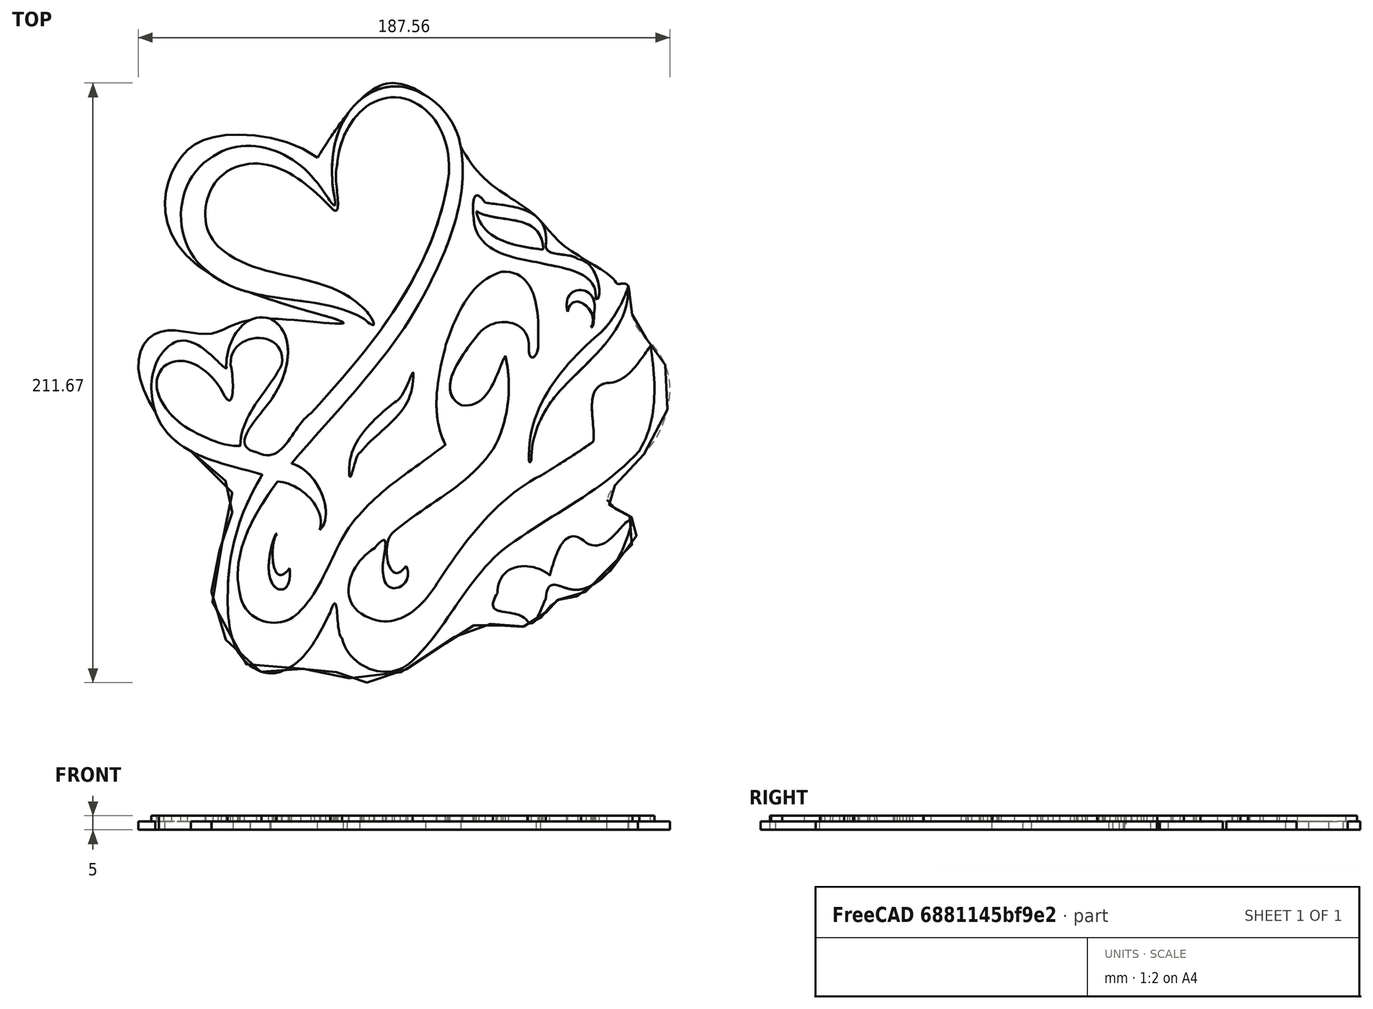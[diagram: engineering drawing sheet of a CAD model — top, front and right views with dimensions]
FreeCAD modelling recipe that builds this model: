
FCSTD DOCUMENT  (FreeCAD 0.20R29410 (Git))
Label: Miriam
License: All rights reserved
LicenseURL: http://en.wikipedia.org/wiki/All_rights_reserved
objects: Part::Feature×9, Sketcher::SketchObject×2, Part::Extrusion×2, PartDesign::Body×1, Part::MultiFuse×1, Mesh::Feature×1
note: 15 computed .brp shape members not serialized (recipe doc carries the construction recipe); baked Part::Feature solids carry a one-line shape summary decoded from their .brp

FEATURE [PartDesign::Body] Body
  Origin = -> Origin
FEATURE [Part::Feature] path198
  shape: bbox 180.5 x 215.9 x 2e-07 mm, 1 faces, 0 solids (baked)
FEATURE [Part::Feature] path198001
  shape: bbox 51.01 x 42.11 x 2e-07 mm, 1 faces, 0 solids (baked)
FEATURE [Part::Feature] path198002
  shape: bbox 53.62 x 39.98 x 2e-07 mm, 1 faces, 0 solids (baked)
FEATURE [Part::Feature] path198003
  shape: bbox 11.12 x 21.68 x 2e-07 mm, 1 faces, 0 solids (baked)
FEATURE [Part::Feature] path198004
  shape: bbox 23.9 x 49.31 x 2e-07 mm, 1 faces, 0 solids (baked)
FEATURE [Part::Feature] path198005
  shape: bbox 35.84 x 63.97 x 2e-07 mm, 1 faces, 0 solids (baked)
FEATURE [Part::Feature] path198006
  shape: bbox 14.27 x 15.77 x 2e-07 mm, 1 faces, 0 solids (baked)
FEATURE [Part::Feature] path198007
  shape: bbox 47.43 x 42.63 x 2e-07 mm, 1 faces, 0 solids (baked)
FEATURE [Part::Feature] path198008
  shape: bbox 23.68 x 13.52 x 2e-07 mm, 1 faces, 0 solids (baked)
FEATURE [Sketcher::SketchObject] Sketch
  FullyConstrained = false
  sketch-geometry (94):
    g0: BSplineCurve PolesCount=4 KnotsCount=2 Degree=3 IsPeriodic=0
    g1: BSplineCurve PolesCount=4 KnotsCount=2 Degree=3 IsPeriodic=0
    g2: BSplineCurve PolesCount=4 KnotsCount=2 Degree=3 IsPeriodic=0
    g3: BSplineCurve PolesCount=4 KnotsCount=2 Degree=3 IsPeriodic=0
    g4: BSplineCurve PolesCount=4 KnotsCount=2 Degree=3 IsPeriodic=0
    g5: BSplineCurve PolesCount=4 KnotsCount=2 Degree=3 IsPeriodic=0
    g6: BSplineCurve PolesCount=4 KnotsCount=2 Degree=3 IsPeriodic=0
    g7: BSplineCurve PolesCount=4 KnotsCount=2 Degree=3 IsPeriodic=0
    g8: BSplineCurve PolesCount=4 KnotsCount=2 Degree=3 IsPeriodic=0
    g9: BSplineCurve PolesCount=4 KnotsCount=2 Degree=3 IsPeriodic=0
    g10: BSplineCurve PolesCount=4 KnotsCount=2 Degree=3 IsPeriodic=0
    g11: BSplineCurve PolesCount=4 KnotsCount=2 Degree=3 IsPeriodic=0
    g12: BSplineCurve PolesCount=4 KnotsCount=2 Degree=3 IsPeriodic=0
    g13: BSplineCurve PolesCount=4 KnotsCount=2 Degree=3 IsPeriodic=0
    g14: BSplineCurve PolesCount=4 KnotsCount=2 Degree=3 IsPeriodic=0
    g15: BSplineCurve PolesCount=4 KnotsCount=2 Degree=3 IsPeriodic=0
    g16: BSplineCurve PolesCount=4 KnotsCount=2 Degree=3 IsPeriodic=0
    g17: BSplineCurve PolesCount=4 KnotsCount=2 Degree=3 IsPeriodic=0
    g18: BSplineCurve PolesCount=4 KnotsCount=2 Degree=3 IsPeriodic=0
    g19: BSplineCurve PolesCount=4 KnotsCount=2 Degree=3 IsPeriodic=0
    g20: BSplineCurve PolesCount=4 KnotsCount=2 Degree=3 IsPeriodic=0
    g21: BSplineCurve PolesCount=4 KnotsCount=2 Degree=3 IsPeriodic=0
    g22: BSplineCurve PolesCount=4 KnotsCount=2 Degree=3 IsPeriodic=0
    g23: BSplineCurve PolesCount=4 KnotsCount=2 Degree=3 IsPeriodic=0
    g24: BSplineCurve PolesCount=4 KnotsCount=2 Degree=3 IsPeriodic=0
    g25: BSplineCurve PolesCount=4 KnotsCount=2 Degree=3 IsPeriodic=0
    g26: BSplineCurve PolesCount=4 KnotsCount=2 Degree=3 IsPeriodic=0
    g27: BSplineCurve PolesCount=4 KnotsCount=2 Degree=3 IsPeriodic=0
    g28: BSplineCurve PolesCount=4 KnotsCount=2 Degree=3 IsPeriodic=0
    g29: BSplineCurve PolesCount=4 KnotsCount=2 Degree=3 IsPeriodic=0
    g30: BSplineCurve PolesCount=4 KnotsCount=2 Degree=3 IsPeriodic=0
    g31: BSplineCurve PolesCount=4 KnotsCount=2 Degree=3 IsPeriodic=0
    g32: BSplineCurve PolesCount=4 KnotsCount=2 Degree=3 IsPeriodic=0
    g33: BSplineCurve PolesCount=4 KnotsCount=2 Degree=3 IsPeriodic=0
    g34: BSplineCurve PolesCount=4 KnotsCount=2 Degree=3 IsPeriodic=0
    g35: BSplineCurve PolesCount=4 KnotsCount=2 Degree=3 IsPeriodic=0
    g36: BSplineCurve PolesCount=4 KnotsCount=2 Degree=3 IsPeriodic=0
    g37: BSplineCurve PolesCount=4 KnotsCount=2 Degree=3 IsPeriodic=0
    g38: BSplineCurve PolesCount=4 KnotsCount=2 Degree=3 IsPeriodic=0
    g39: BSplineCurve PolesCount=4 KnotsCount=2 Degree=3 IsPeriodic=0
    g40: BSplineCurve PolesCount=4 KnotsCount=2 Degree=3 IsPeriodic=0
    g41: BSplineCurve PolesCount=4 KnotsCount=2 Degree=3 IsPeriodic=0
    g42: BSplineCurve PolesCount=4 KnotsCount=2 Degree=3 IsPeriodic=0
    g43: BSplineCurve PolesCount=4 KnotsCount=2 Degree=3 IsPeriodic=0
    g44: BSplineCurve PolesCount=4 KnotsCount=2 Degree=3 IsPeriodic=0
    g45: BSplineCurve PolesCount=4 KnotsCount=2 Degree=3 IsPeriodic=0
    g46: BSplineCurve PolesCount=4 KnotsCount=2 Degree=3 IsPeriodic=0
    g47: BSplineCurve PolesCount=4 KnotsCount=2 Degree=3 IsPeriodic=0
    g48: BSplineCurve PolesCount=4 KnotsCount=2 Degree=3 IsPeriodic=0
    g49: BSplineCurve PolesCount=4 KnotsCount=2 Degree=3 IsPeriodic=0
    g50: BSplineCurve PolesCount=4 KnotsCount=2 Degree=3 IsPeriodic=0
    g51: BSplineCurve PolesCount=4 KnotsCount=2 Degree=3 IsPeriodic=0
    g52: BSplineCurve PolesCount=4 KnotsCount=2 Degree=3 IsPeriodic=0
    g53: BSplineCurve PolesCount=4 KnotsCount=2 Degree=3 IsPeriodic=0
    g54: BSplineCurve PolesCount=4 KnotsCount=2 Degree=3 IsPeriodic=0
    g55: BSplineCurve PolesCount=4 KnotsCount=2 Degree=3 IsPeriodic=0
    g56: BSplineCurve PolesCount=4 KnotsCount=2 Degree=3 IsPeriodic=0
    g57: BSplineCurve PolesCount=4 KnotsCount=2 Degree=3 IsPeriodic=0
    g58: BSplineCurve PolesCount=4 KnotsCount=2 Degree=3 IsPeriodic=0
    g59: BSplineCurve PolesCount=4 KnotsCount=2 Degree=3 IsPeriodic=0
    g60: BSplineCurve PolesCount=4 KnotsCount=2 Degree=3 IsPeriodic=0
    g61: BSplineCurve PolesCount=4 KnotsCount=2 Degree=3 IsPeriodic=0
    g62: BSplineCurve PolesCount=2 KnotsCount=2 Degree=1 IsPeriodic=0
    g63: BSplineCurve PolesCount=4 KnotsCount=2 Degree=3 IsPeriodic=0
    g64: BSplineCurve PolesCount=4 KnotsCount=2 Degree=3 IsPeriodic=0
    g65: BSplineCurve PolesCount=4 KnotsCount=2 Degree=3 IsPeriodic=0
    g66: BSplineCurve PolesCount=4 KnotsCount=2 Degree=3 IsPeriodic=0
    g67: BSplineCurve PolesCount=4 KnotsCount=2 Degree=3 IsPeriodic=0
    g68: BSplineCurve PolesCount=4 KnotsCount=2 Degree=3 IsPeriodic=0
    g69: BSplineCurve PolesCount=4 KnotsCount=2 Degree=3 IsPeriodic=0
    g70: BSplineCurve PolesCount=4 KnotsCount=2 Degree=3 IsPeriodic=0
    g71: BSplineCurve PolesCount=4 KnotsCount=2 Degree=3 IsPeriodic=0
    g72: BSplineCurve PolesCount=4 KnotsCount=2 Degree=3 IsPeriodic=0
    g73: BSplineCurve PolesCount=4 KnotsCount=2 Degree=3 IsPeriodic=0
    g74: BSplineCurve PolesCount=4 KnotsCount=2 Degree=3 IsPeriodic=0
    g75: BSplineCurve PolesCount=4 KnotsCount=2 Degree=3 IsPeriodic=0
    g76: BSplineCurve PolesCount=4 KnotsCount=2 Degree=3 IsPeriodic=0
    g77: BSplineCurve PolesCount=4 KnotsCount=2 Degree=3 IsPeriodic=0
    g78: BSplineCurve PolesCount=4 KnotsCount=2 Degree=3 IsPeriodic=0
    g79: BSplineCurve PolesCount=4 KnotsCount=2 Degree=3 IsPeriodic=0
    g80: BSplineCurve PolesCount=4 KnotsCount=2 Degree=3 IsPeriodic=0
    g81: BSplineCurve PolesCount=4 KnotsCount=2 Degree=3 IsPeriodic=0
    g82: BSplineCurve PolesCount=4 KnotsCount=2 Degree=3 IsPeriodic=0
    g83: BSplineCurve PolesCount=4 KnotsCount=2 Degree=3 IsPeriodic=0
    g84: BSplineCurve PolesCount=4 KnotsCount=2 Degree=3 IsPeriodic=0
    g85: BSplineCurve PolesCount=4 KnotsCount=2 Degree=3 IsPeriodic=0
    g86: BSplineCurve PolesCount=4 KnotsCount=2 Degree=3 IsPeriodic=0
    g87: BSplineCurve PolesCount=4 KnotsCount=2 Degree=3 IsPeriodic=0
    g88: BSplineCurve PolesCount=4 KnotsCount=2 Degree=3 IsPeriodic=0
    g89: BSplineCurve PolesCount=4 KnotsCount=2 Degree=3 IsPeriodic=0
    g90: BSplineCurve PolesCount=4 KnotsCount=2 Degree=3 IsPeriodic=0
    g91: BSplineCurve PolesCount=4 KnotsCount=2 Degree=3 IsPeriodic=0
    g92: BSplineCurve PolesCount=4 KnotsCount=2 Degree=3 IsPeriodic=0
    g93: BSplineCurve PolesCount=2 KnotsCount=2 Degree=1 IsPeriodic=0
  constraints (94):
    c: Coincident(g0,g1)
    c: Coincident(g1,g2)
    c: Coincident(g2,g3)
    c: Coincident(g3,g4)
    c: Coincident(g4,g5)
    c: Coincident(g5,g6)
    c: Coincident(g6,g7)
    c: Coincident(g7,g8)
    c: Coincident(g8,g9)
    c: Coincident(g9,g10)
    c: Coincident(g10,g11)
    c: Coincident(g11,g12)
    c: Coincident(g12,g13)
    c: Coincident(g13,g14)
    c: Coincident(g14,g15)
    c: Coincident(g15,g16)
    c: Coincident(g16,g17)
    c: Coincident(g17,g18)
    c: Coincident(g18,g19)
    c: Coincident(g19,g20)
    c: Coincident(g20,g21)
    c: Coincident(g21,g22)
    c: Coincident(g22,g23)
    c: Coincident(g23,g24)
    c: Coincident(g24,g25)
    c: Coincident(g25,g26)
    c: Coincident(g26,g27)
    c: Coincident(g27,g28)
    c: Coincident(g28,g29)
    c: Coincident(g29,g30)
    c: Coincident(g30,g31)
    c: Coincident(g31,g32)
    c: Coincident(g32,g33)
    c: Coincident(g33,g34)
    c: Coincident(g34,g35)
    c: Coincident(g35,g36)
    c: Coincident(g36,g37)
    c: Coincident(g37,g38)
    c: Coincident(g38,g39)
    c: Coincident(g39,g40)
    c: Coincident(g40,g41)
    c: Coincident(g41,g42)
    c: Coincident(g42,g43)
    c: Coincident(g43,g44)
    c: Coincident(g44,g45)
    c: Coincident(g45,g46)
    c: Coincident(g46,g47)
    c: Coincident(g47,g48)
    c: Coincident(g48,g49)
    c: Coincident(g49,g50)
    c: Coincident(g50,g51)
    c: Coincident(g51,g52)
    c: Coincident(g52,g53)
    c: Coincident(g53,g54)
    c: Coincident(g54,g55)
    c: Coincident(g55,g0)
    c: Coincident(g56,g57)
    c: Coincident(g57,g58)
    c: Coincident(g58,g59)
    c: Coincident(g59,g60)
    c: Coincident(g60,g61)
    c: Coincident(g61,g62)
    c: Coincident(g62,g56)
    c: Coincident(g63,g64)
    c: Coincident(g64,g65)
    c: Coincident(g65,g66)
    c: Coincident(g66,g67)
    c: Coincident(g67,g68)
    c: Coincident(g68,g69)
    c: Coincident(g69,g63)
    c: Coincident(g70,g71)
    c: Coincident(g71,g72)
    c: Coincident(g72,g70)
    c: Coincident(g73,g74)
    c: Coincident(g74,g75)
    c: Coincident(g75,g76)
    c: Coincident(g76,g73)
    c: Coincident(g77,g78)
    c: Coincident(g78,g79)
    c: Coincident(g79,g80)
    c: Coincident(g80,g81)
    c: Coincident(g81,g77)
    c: Coincident(g82,g83)
    c: Coincident(g83,g84)
    c: Coincident(g84,g82)
    c: Coincident(g85,g86)
    c: Coincident(g86,g87)
    c: Coincident(g87,g88)
    c: Coincident(g88,g89)
    c: Coincident(g89,g90)
    c: Coincident(g90,g85)
    c: Coincident(g91,g92)
    c: Coincident(g92,g93)
    c: Coincident(g93,g91)
FEATURE [Part::Extrusion] Extrude
  Base = -> Sketch
  Dir = (0,0,1)
  DirMode = 2
  FaceMakerClass = Part::FaceMakerBullseye
  LengthFwd = 5
  LengthRev = 0
  Solid = true
  Symmetric = false
FEATURE [Sketcher::SketchObject] Sketch001
  FullyConstrained = false
  MapMode = 2
  Support = -> [Extrude]
  sketch-geometry (85):
    g0-g42: Circle x43 (B-spline internal-alignment scaffolding for g43; pole/knot coordinates omitted)
    g43: BSplineCurve PolesCount=43 KnotsCount=41 Degree=3 IsPeriodic=0
    g44-g84: GeomPoint x41 (B-spline internal-alignment scaffolding for g43; pole/knot coordinates omitted)
  constraints (5):
    c: Weight(g0) = 1
    c: Equal(g0, g1-g42) x42
    c: Coincident(g43,g0)
    c: InternalAlignment(g0-g42 -> g43) x43
    c: InternalAlignment(g44-g84 -> g43) x41
FEATURE [Part::Extrusion] Extrude001
  Base = -> Sketch001
  Dir = (0,0,1)
  DirMode = 2
  FaceMakerClass = Part::FaceMakerBullseye
  LengthFwd = 3
  LengthRev = 0
  Solid = true
  Symmetric = false
FEATURE [Part::MultiFuse] Fusion  label="miriam"
  Refine = true
  Shapes = -> [Extrude,Extrude001]
FEATURE [Mesh::Feature] Mesh  label="miriam (Meshed)"
